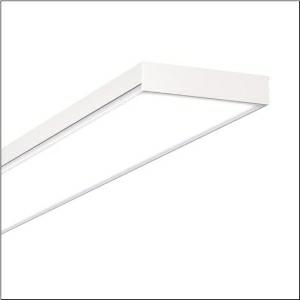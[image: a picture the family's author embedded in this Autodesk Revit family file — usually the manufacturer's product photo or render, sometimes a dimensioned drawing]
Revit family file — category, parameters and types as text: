
# Revit family: apollon_31_surface_51mp26wm2341w
name_source: partatom
category: Lighting Fixtures
units: mm (PartAtom-declared; Revit-internal decimal feet)

## family parameters
Cut with Voids When Loaded = No
Host = Face
Light Source = No
Part Type = Normal
Room Calculation Point = No
Round Connector Dimension = Use Diameter
Shared = No

## types (1)
- Apollon 31 Surface (1 x LED, 4400 lm, 33 W, 3000K)
    Apparent Load = 33 VA
    CIE Flux Codes = 61 87 97 97 100
    Color Rendering = 80
    Color Temperature = 3000K
    Default Elevation = 1800 mm
    Description = Apollon 31 Surface, office luminaire, primary optical cover: micro prismatic cover, of PMMA, light emission: direct distribution, primary light characteristic: symmetric, installation type: surface-mounted, LED, rated luminous flux: 4.400lm, luminous efficacy: 133lm/W, light colour: 830, colour temperature: 3000K, control gear: ON/OFF Multilumen, with terminal, 3-pole, mains connection: 220..240V, AC, 50/60Hz, rated input power: 33W, housing, of sheet steel, coated, traffic white (RAL 9016), length: 1.545mm, width: 200mm, height: 44mm, protection rating (complete): IP20, protection rating (on room side): IP40, protection rating (lamp compartment, on room side): IP40, insulation class (complete): insulation class I (protective earthing), certification: CE, ENEC, UKCA, impact resistance: IK02, permissible operating ambient temperature: -20..+40°C, packaging unit: 1 piece
    Height = 44 mm
    Lamp = 1 x LED
    Lamp Light Flux = 4400 lm
    Lamp Power = 33 W
    Lamp count = 1
    Length = 1545 mm
    Luminous efficacy = 133 lm/W
    Manufacturer = Siteco
    ModVariant = No
    Model = 51MP26WM2341W
    Mounting Place = Ceiling
    Mounting Type = Surface mounted
    Number of Poles = 1
    OnlyDefault = Yes
    Power Factor = 1
    Product Name = Apollon 31 Surface
    Product group = office luminaire | ceiling mounted
    ProductGroupID = 301
    Protection Class = Protection class I
    Protection Degree = IP 20
    RLX_Detail_Level = 1
    RLX_Emergency_Light_Flux = 0 lm
    RLX_Emergency_Type = 0
    RLX_Emergency_Type_DB = No
    RlxData = <blob elided: 20829 chars, md5=c8835fba>
    Socket = socket
    Standby Power = 0 W
    System Light Flux = 4400 lm
    System Power = 33 W
    Type Comments = Product without accessories
    Type Image = l_1313658.jpg
    URL = http://relux.com
    VarID = ---
    Voltage = 0 V
    Weight = 0.00 kg
    Width = 200 mm  [stored 0.656168 ft]

note: [stored X ft] marks values corroborated as IEEE doubles in the binary element streams (Revit-internal decimal feet)

## geometry (parser evidence)
native form markers: Blend x4, Sweep x11
no freeform markers — native parametric forms only
